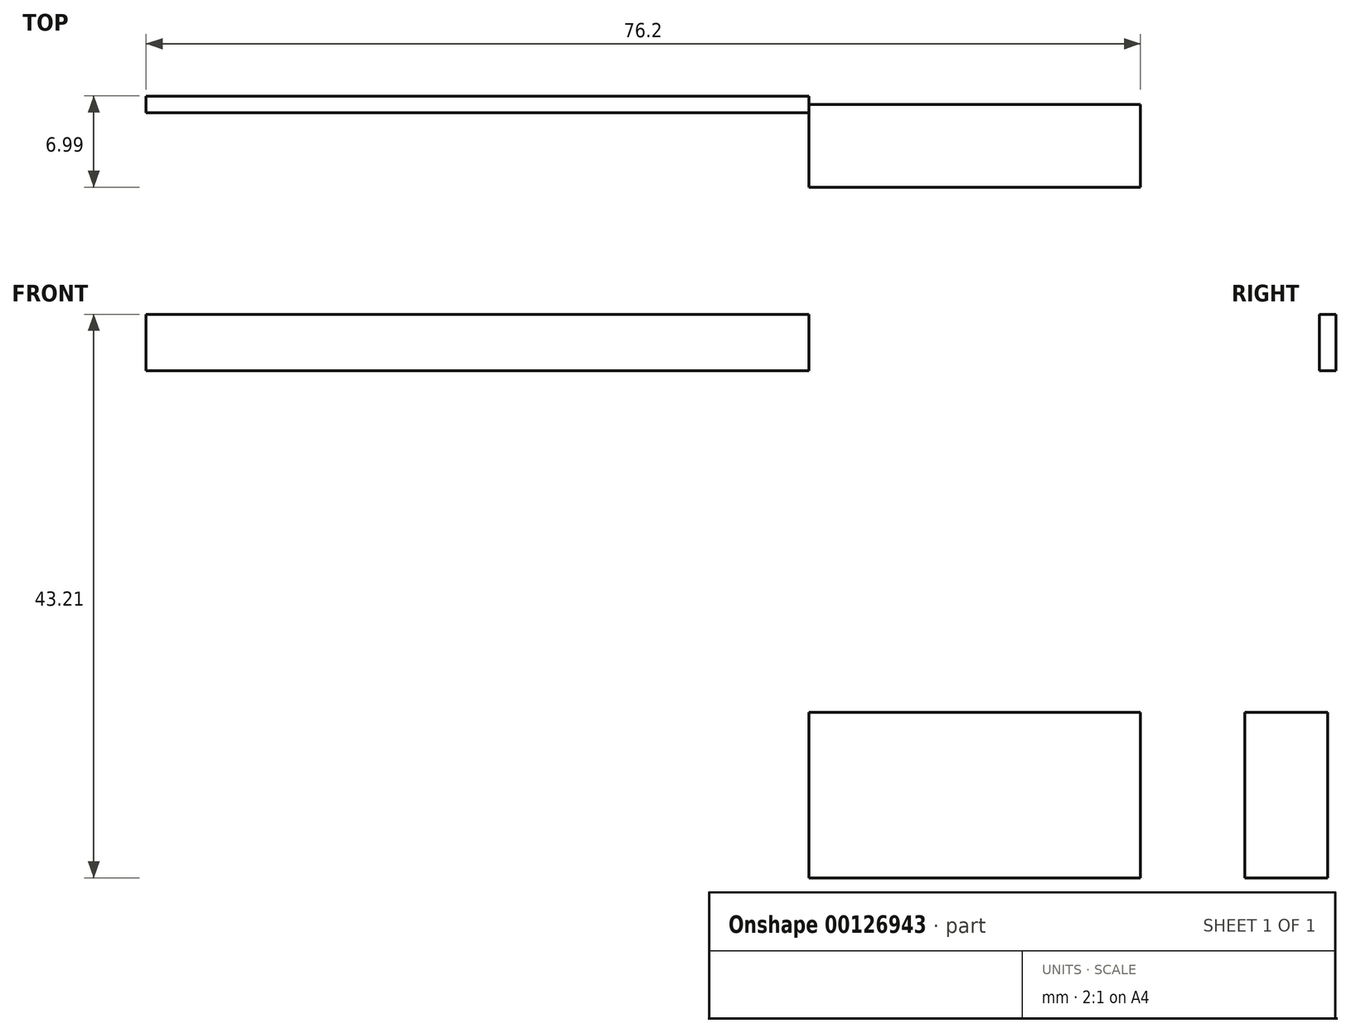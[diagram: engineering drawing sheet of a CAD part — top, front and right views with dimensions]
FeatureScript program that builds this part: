
annotation { "Feature Type Name" : "Feature", "Feature Type Description" : "" }
export const myFeature = defineFeature(function(context is Context, id is Id, definition is map)
    precondition{}
    {
        {
            var Q0;
            Q0=qCreatedBy(makeId("Front.planeOp"),FACE);
            var sketch = newSketch(context, id + "F0", { "sketchPlane" : qUnion([Q0])});
            skLineSegment(sketch, "E0.bottom", {"start": v(0, 0) * mm, "end": v(25.4, 0) * mm});
            skLineSegment(sketch, "E0.top", {"start": v(0, 12.7) * mm, "end": v(25.4, 12.7) * mm});
            skLineSegment(sketch, "E0.left", {"start": v(0, 0) * mm, "end": v(0, 12.7) * mm});
            skLineSegment(sketch, "E0.right", {"start": v(25.4, 0) * mm, "end": v(25.4, 12.7) * mm});
            skSolve(sketch);
        }
        {
            var Q0;
            Q0=makeQuery(id+"F0.imprint","IMPRINT",FACE,{"disambiguationData":[TD([[makeQuery(id+"F0.imprint","IMPRINT",EDGE,{"derivedFrom":sQuery(id+"F0.wireOp",EDGE,"E0.bottom")}),1.0]])]});
            extrude(context, id + "F1", {"entities" : qUnion([Q0]), "depth" : 6.35 * mm});
        }
        {
            var Q0;
            Q0=qCreatedBy(makeId("Front.planeOp"),FACE);
            var sketch = newSketch(context, id + "F2", { "sketchPlane" : qUnion([Q0])});
            skLineSegment(sketch, "E1.bottom", {"start": v(-50.8, 43.21) * mm, "end": v(0, 43.21) * mm});
            skLineSegment(sketch, "E1.top", {"start": v(-50.8, 38.88) * mm, "end": v(0, 38.88) * mm});
            skLineSegment(sketch, "E1.left", {"start": v(-50.8, 43.21) * mm, "end": v(-50.8, 38.88) * mm});
            skLineSegment(sketch, "E1.right", {"start": v(0, 43.21) * mm, "end": v(0, 38.88) * mm});
            skSolve(sketch);
        }
        {
            var Q0;
            Q0=makeQuery(id+"F2.imprint","IMPRINT",FACE,{"disambiguationData":[TD([[makeQuery(id+"F2.imprint","IMPRINT",EDGE,{"derivedFrom":sQuery(id+"F2.wireOp",EDGE,"E1.bottom")}),-1.0]])]});
            extrude(context, id + "F3", {"entities" : qUnion([Q0]), "endBound" : BoundingType.SYMMETRIC, "depth" : 1.27 * mm});
        }
    });
